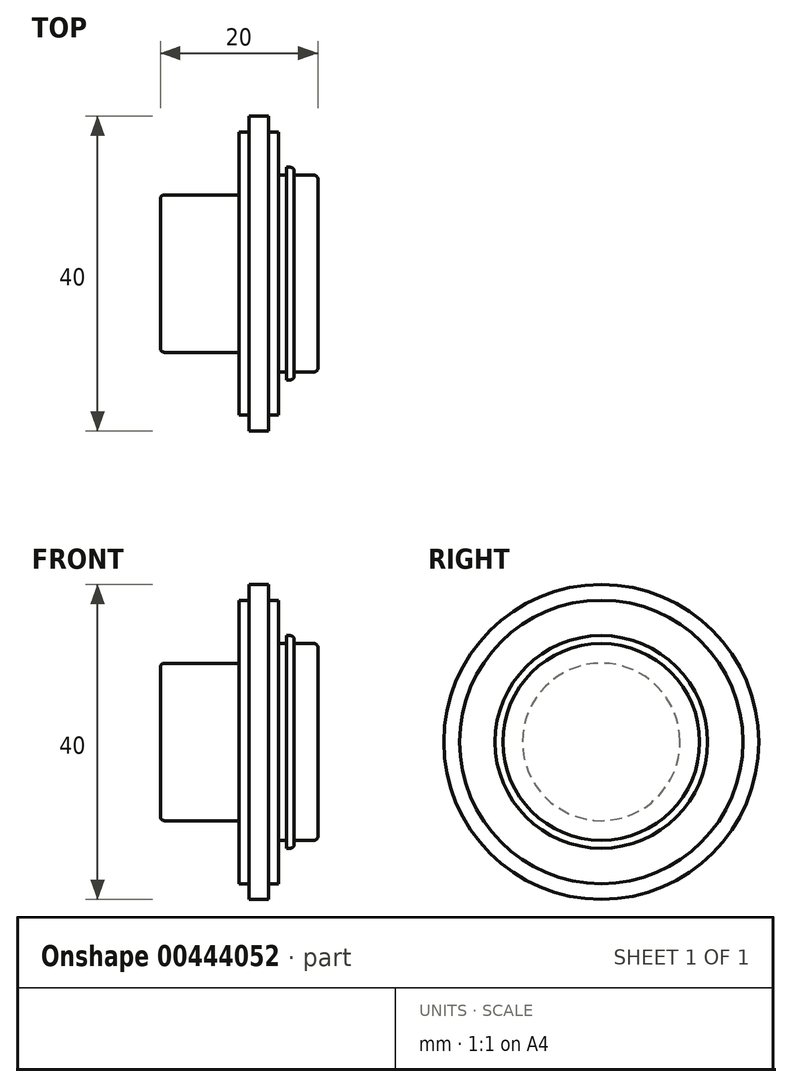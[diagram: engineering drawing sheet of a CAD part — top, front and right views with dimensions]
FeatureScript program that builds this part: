
annotation { "Feature Type Name" : "Feature", "Feature Type Description" : "" }
export const myFeature = defineFeature(function(context is Context, id is Id, definition is map)
    precondition{}
    {
        {
            var Q0;
            Q0=qCreatedBy(makeId("Front.planeOp"),FACE);
            var sketch = newSketch(context, id + "F0", { "sketchPlane" : qUnion([Q0])});
            skLineSegment(sketch, "E0", {"start": v(0, 0) * mm, "end": v(-20, 0) * mm});
            skLineSegment(sketch, "E1", {"start": v(-20, 0) * mm, "end": v(-20, 10) * mm});
            skLineSegment(sketch, "E2", {"start": v(-20, 10) * mm, "end": v(-10, 10) * mm});
            skLineSegment(sketch, "E3", {"start": v(-10, 10) * mm, "end": v(-10, 18) * mm});
            skLineSegment(sketch, "E4", {"start": v(-10, 18) * mm, "end": v(-8.75, 18) * mm});
            skLineSegment(sketch, "E5", {"start": v(-8.75, 18) * mm, "end": v(-8.75, 20) * mm});
            skLineSegment(sketch, "E6", {"start": v(-8.75, 20) * mm, "end": v(-8.75, 20) * mm});
            skLineSegment(sketch, "E7", {"start": v(-8.75, 20) * mm, "end": v(-8.75, 18) * mm});
            skLineSegment(sketch, "E8", {"start": v(-5, 18) * mm, "end": v(-5, 12.5) * mm});
            skLineSegment(sketch, "E9", {"start": v(-5, 12.5) * mm, "end": v(-4, 12.5) * mm});
            skLineSegment(sketch, "E10", {"start": v(-4, 12.5) * mm, "end": v(-4, 13.5) * mm});
            skLineSegment(sketch, "E11", {"start": v(-4, 13.5) * mm, "end": v(-3, 13.5) * mm});
            skLineSegment(sketch, "E12", {"start": v(-3, 13.5) * mm, "end": v(-3, 12.5) * mm});
            skLineSegment(sketch, "E13", {"start": v(-3, 12.5) * mm, "end": v(0, 12.5) * mm});
            skLineSegment(sketch, "E14", {"start": v(0, 12.5) * mm, "end": v(0, 0) * mm});
            skLineSegment(sketch, "E15", {"start": v(-8.75, 20) * mm, "end": v(-6.25, 20) * mm});
            skLineSegment(sketch, "E16", {"start": v(-6.25, 20) * mm, "end": v(-6.25, 18) * mm});
            skLineSegment(sketch, "E17", {"start": v(-6.25, 18) * mm, "end": v(-5, 18) * mm});
            skSolve(sketch);
        }
        {
            var Q0;
            Q0 = qSketchRegion(id + "F0", true);
            var Q1;
            Q1=sQuery(id+"F0.wireOp",EDGE,"E0");
            revolve(context, id + "F1", {"entities" : qUnion([Q0]), "axis" : qUnion([Q1]), "revolveType" : RevolveType.FULL});
        }
        {
            var Q0;
            Q0=makeQuery(id+"F1.opRevolve","SWEPT_EDGE",EDGE,{"disambiguationData":[OSD([sQuery(id+"F0.wireOp",EDGE,"E1"),sQuery(id+"F0.wireOp",EDGE,"E2")])]});
            var Q1;
            Q1=makeQuery(id+"F1.opRevolve","SWEPT_EDGE",EDGE,{"disambiguationData":[OSD([sQuery(id+"F0.wireOp",EDGE,"E11"),sQuery(id+"F0.wireOp",EDGE,"E12")])]});
            var Q2;
            Q2=makeQuery(id+"F1.opRevolve","SWEPT_EDGE",EDGE,{"disambiguationData":[OSD([sQuery(id+"F0.wireOp",EDGE,"E13"),sQuery(id+"F0.wireOp",EDGE,"E14")])]});
            fillet(context, id + "F2", {"entities" : qUnion([Q0, Q1, Q2]), "radius" : 0.5 * mm, "tangentPropagation" : true, "allowEdgeOverflow" : false});
        }
    });
